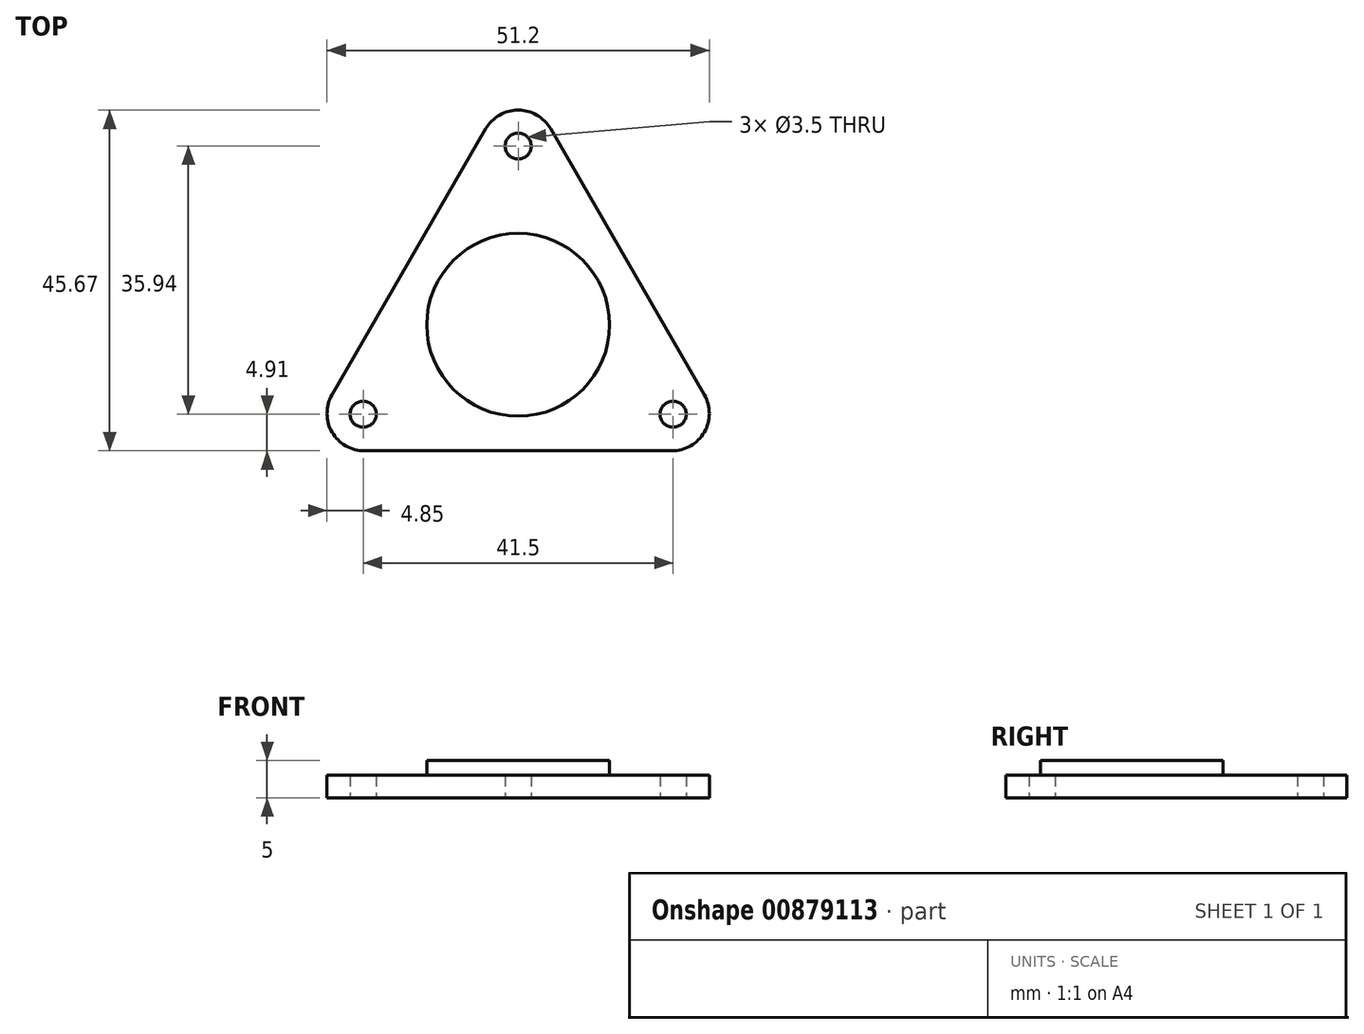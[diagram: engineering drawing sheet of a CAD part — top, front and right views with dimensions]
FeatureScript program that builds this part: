
annotation { "Feature Type Name" : "Feature", "Feature Type Description" : "" }
export const myFeature = defineFeature(function(context is Context, id is Id, definition is map)
    precondition{}
    {
        {
            var Q0;
            Q0=qCreatedBy(makeId("Top.planeOp"),FACE);
            var sketch = newSketch(context, id + "F0", { "sketchPlane" : qUnion([Q0])});
            skCircle(sketch, "E0.cCircle", {"center": v(0, 0) * mm, "radius": 23.96 * mm, "construction": true});
            skLineSegment(sketch, "E0.0", {"start": v(0, 23.96) * mm, "end": v(20.75, -11.98) * mm, "construction": true});
            skLineSegment(sketch, "E0.1", {"start": v(20.75, -11.98) * mm, "end": v(-20.75, -11.98) * mm, "construction": true});
            skLineSegment(sketch, "E0.2", {"start": v(-20.75, -11.98) * mm, "end": v(0, 23.96) * mm, "construction": true});
            skCircle(sketch, "E1.cCircle", {"center": v(0, 0) * mm, "radius": 33.78 * mm, "construction": true});
            skLineSegment(sketch, "E1.0", {"start": v(4.33, 26.28) * mm, "end": v(24.93, -9.4) * mm});
            skLineSegment(sketch, "E1.1", {"start": v(20.6, -16.9) * mm, "end": v(-20.6, -16.9) * mm});
            skLineSegment(sketch, "E1.2", {"start": v(-24.93, -9.4) * mm, "end": v(-4.33, 26.28) * mm});
            skCircle(sketch, "E2", {"center": v(0, 23.96) * mm, "radius": 1.75 * mm});
            skCircle(sketch, "E3", {"center": v(-20.75, -11.98) * mm, "radius": 1.75 * mm});
            skCircle(sketch, "E4", {"center": v(20.75, -11.98) * mm, "radius": 1.75 * mm});
            skPoint(sketch, "E5.visualSharp", {"position": v(0, 33.78) * mm});
            skArc(sketch, "E5.filletArc", {"start": v(4.33, 26.28) * mm, "mid": v(0, 28.78) * mm, "end": v(-4.33, 26.28) * mm});
            skPoint(sketch, "E6.visualSharp", {"position": v(29.26, -16.9) * mm});
            skArc(sketch, "E6.filletArc", {"start": v(20.6, -16.9) * mm, "mid": v(24.93, -14.4) * mm, "end": v(24.93, -9.4) * mm});
            skPoint(sketch, "E7.visualSharp", {"position": v(-29.26, -16.9) * mm});
            skArc(sketch, "E7.filletArc", {"start": v(-24.93, -9.4) * mm, "mid": v(-24.93, -14.4) * mm, "end": v(-20.6, -16.9) * mm});
            skSolve(sketch);
        }
        {
            var Q0;
            Q0=makeQuery(id+"F0.imprint","IMPRINT",FACE,{"disambiguationData":[TD([[makeQuery(id+"F0.imprint","IMPRINT",EDGE,{"derivedFrom":sQuery(id+"F0.wireOp",EDGE,"E1.0")}),-1.0]])]});
            extrude(context, id + "F1", {"entities" : qUnion([Q0]), "depth" : 3 * mm, "offsetDistance" : 25 * mm});
        }
        {
            var Q0;
            Q0=makeQuery(id+"F1.opExtrude","CAP_FACE",FACE,{"disambiguationData":[OSD([sQuery(id+"F0.wireOp",EDGE,"E1.0"),sQuery(id+"F0.wireOp",EDGE,"E1.1"),sQuery(id+"F0.wireOp",EDGE,"E1.2"),sQuery(id+"F0.wireOp",EDGE,"E2"),sQuery(id+"F0.wireOp",EDGE,"E3"),sQuery(id+"F0.wireOp",EDGE,"E4"),sQuery(id+"F0.wireOp",EDGE,"E5.filletArc"),sQuery(id+"F0.wireOp",EDGE,"E6.filletArc"),sQuery(id+"F0.wireOp",EDGE,"E7.filletArc")])],"isStart":false});
            var sketch = newSketch(context, id + "F2", { "sketchPlane" : qUnion([Q0])});
            skCircle(sketch, "E8", {"center": v(0, 0) * mm, "radius": 12.25 * mm});
            skSolve(sketch);
        }
        {
            var Q0;
            Q0 = qSketchRegion(id + "F2", true);
            extrude(context, id + "F3", {"entities" : qUnion([Q0]), "operationType" : NewBodyOperationType.ADD, "depth" : 2 * mm, "offsetDistance" : 25 * mm});
        }
    });
